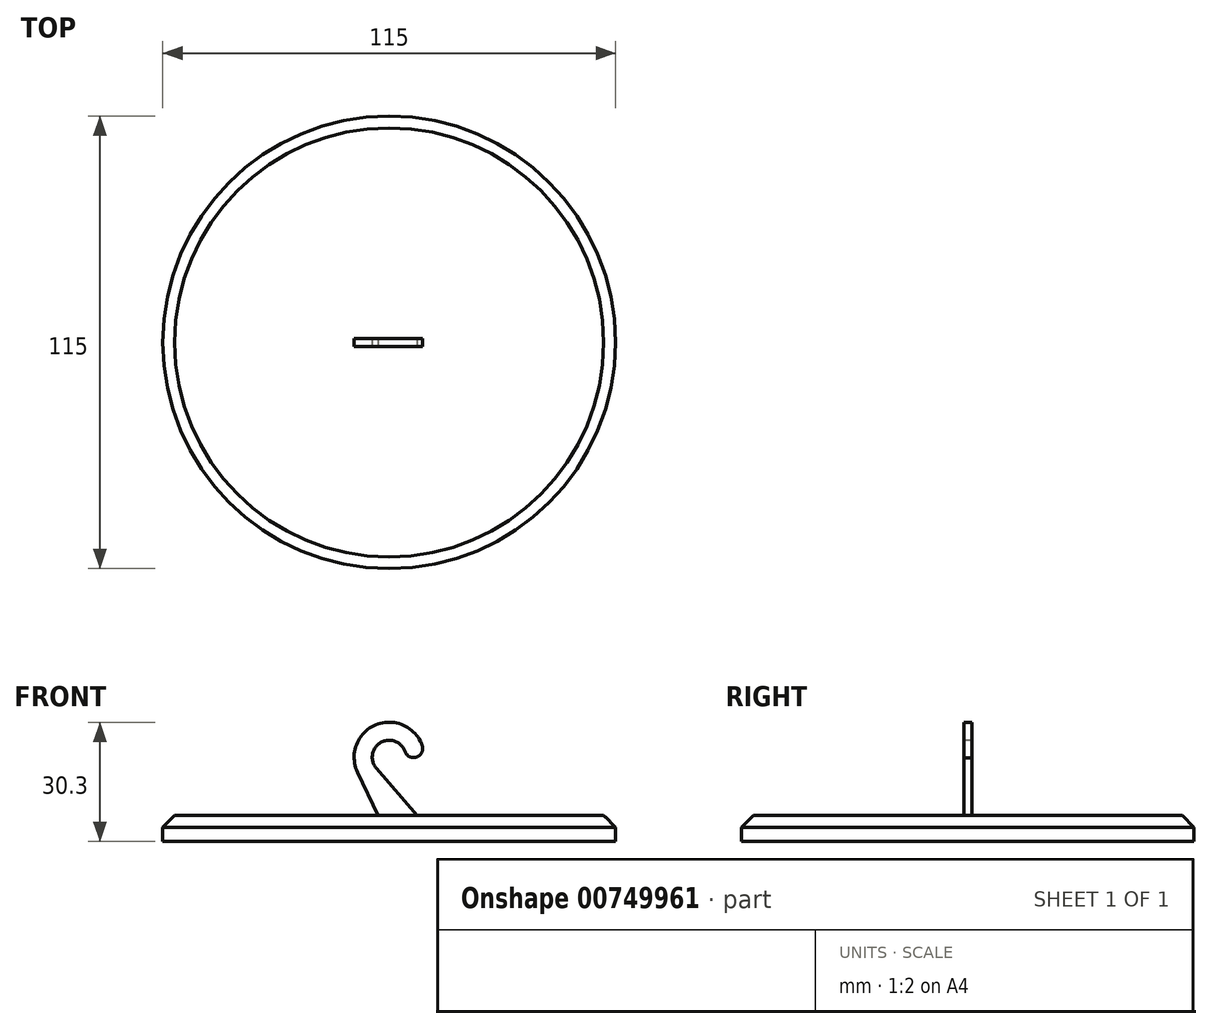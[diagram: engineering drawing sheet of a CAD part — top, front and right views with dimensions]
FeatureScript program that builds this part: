
annotation { "Feature Type Name" : "Feature", "Feature Type Description" : "" }
export const myFeature = defineFeature(function(context is Context, id is Id, definition is map)
    precondition{}
    {
        {
            var Q0;
            Q0=qCreatedBy(makeId("Top.planeOp"),FACE);
            var sketch = newSketch(context, id + "F0", { "sketchPlane" : qUnion([Q0])});
            skCircle(sketch, "E0", {"center": v(0, 0) * mm, "radius": 57.5 * mm});
            skSolve(sketch);
        }
        {
            var Q0;
            Q0=makeQuery(id+"F0.imprint","IMPRINT",FACE,{"disambiguationData":[TD([[makeQuery(id+"F0.imprint","IMPRINT",EDGE,{"derivedFrom":sQuery(id+"F0.wireOp",EDGE,"E0")}),1.0]])]});
            extrude(context, id + "F1", {"entities" : qUnion([Q0]), "depth" : 6.6 * mm, "offsetDistance" : 25 * mm});
        }
        {
            var Q0;
            Q0=makeQuery(id+"F1.opExtrude","CAP_EDGE",EDGE,{"disambiguationData":[OSD([sQuery(id+"F0.wireOp",EDGE,"E0")])],"isStart":false});
            chamfer(context, id + "F2", {"entities" : qUnion([Q0]), "width" : 3 * mm, "tangentPropagation" : true});
        }
        {
            var Q0;
            Q0=makeQuery(id+"F1.opExtrude","CAP_FACE",FACE,{"disambiguationData":[OSD([sQuery(id+"F0.wireOp",EDGE,"E0")])],"isStart":false});
            var sketch = newSketch(context, id + "F3", { "sketchPlane" : qUnion([Q0])});
            skLineSegment(sketch, "E1.bottom", {"start": v(-8.9, 1) * mm, "end": v(8.9, 1) * mm});
            skLineSegment(sketch, "E1.top", {"start": v(-8.9, -1) * mm, "end": v(8.9, -1) * mm});
            skLineSegment(sketch, "E1.left", {"start": v(-8.9, 1) * mm, "end": v(-8.9, -1) * mm});
            skLineSegment(sketch, "E1.right", {"start": v(8.9, 1) * mm, "end": v(8.9, -1) * mm});
            skLineSegment(sketch, "E2", {"start": v(0, 0) * mm, "end": v(0, 1) * mm, "construction": true});
            skLineSegment(sketch, "E3", {"start": v(0, 0) * mm, "end": v(-8.9, 0) * mm, "construction": true});
            skSolve(sketch);
        }
        {
            var Q0;
            Q0=makeQuery(id+"F3.imprint","IMPRINT",FACE,{"disambiguationData":[TD([[makeQuery(id+"F3.imprint","IMPRINT",EDGE,{"derivedFrom":sQuery(id+"F3.wireOp",EDGE,"E1.bottom")}),-1.0]])]});
            extrude(context, id + "F4", {"entities" : qUnion([Q0]), "operationType" : NewBodyOperationType.ADD, "depth" : 23.7 * mm, "offsetDistance" : 25 * mm});
        }
        {
            var Q0;
            Q0=makeQuery(id+"F4.opExtrude","SWEPT_FACE",FACE,{"disambiguationData":[OSD([sQuery(id+"F3.wireOp",EDGE,"E1.top")])]});
            var sketch = newSketch(context, id + "F5", { "sketchPlane" : qUnion([Q0])});
            skCircle(sketch, "E4", {"center": v(0, 21.4) * mm, "radius": 8.9 * mm});
            skCircle(sketch, "E5", {"center": v(0, 21.4) * mm, "radius": 4.3 * mm});
            skCircle(sketch, "E6", {"center": v(6.23, 23.59) * mm, "radius": 2.3 * mm});
            skLineSegment(sketch, "E7", {"start": v(-3.26, 18.6) * mm, "end": v(7.04, 6.6) * mm});
            skLineSegment(sketch, "E8", {"start": v(-8.03, 17.56) * mm, "end": v(-2.8, 6.6) * mm});
            skSolve(sketch);
        }
        {
            var Q0;
            {var subQ0=sQuery(id+"F5.wireOp",EDGE,"E7");var subQ3=sQuery(id+"F3.wireOp",EDGE,"E1.top");var subQ6=makeQuery(id+"F4.opExtrude","CAP_EDGE",EDGE,{"disambiguationData":[OSD([subQ3])],"isStart":true});var subQ8=makeQuery(id+"F5.imprint","INTERSECT",VERTEX,{"derivedFrom":[subQ6,subQ0]});Q0=makeQuery(id+"F5.imprint","IMPRINT",FACE,{"disambiguationData":[TD([[makeQuery(id+"F5.imprint","IMPRINT",EDGE,{"disambiguationData":[TD([[subQ8,1.0]])],"derivedFrom":subQ0}),1.0]])]});}
            var Q1;
            {var subQ3=sQuery(id+"F5.wireOp",EDGE,"E5");var subQ5=sQuery(id+"F5.wireOp",EDGE,"E7");var subQ6=makeQuery(id+"F5.imprint","INTERSECT",VERTEX,{"derivedFrom":[subQ3,subQ5]});Q1=makeQuery(id+"F5.imprint","IMPRINT",FACE,{"disambiguationData":[TD([[makeQuery(id+"F5.imprint","IMPRINT",EDGE,{"disambiguationData":[TD([[subQ6,-1.0]])],"derivedFrom":subQ3}),-1.0]])]});}
            var Q2;
            {var subQ0=sQuery(id+"F5.wireOp",EDGE,"E5");var subQ1=makeQuery(id+"F5.imprint","INTERSECT",VERTEX,{"derivedFrom":[subQ0,sQuery(id+"F5.wireOp",EDGE,"E7")]});Q2=makeQuery(id+"F5.imprint","IMPRINT",FACE,{"disambiguationData":[TD([[makeQuery(id+"F5.imprint","IMPRINT",EDGE,{"disambiguationData":[TD([[subQ1,1.0]])],"derivedFrom":subQ0}),1.0]])]});}
            var Q3;
            {var subQ0=sQuery(id+"F5.wireOp",EDGE,"E4");var subQ1=makeQuery(id+"F5.imprint","INTERSECT",VERTEX,{"derivedFrom":[subQ0,sQuery(id+"F5.wireOp",EDGE,"E6")]});Q3=makeQuery(id+"F5.imprint","IMPRINT",FACE,{"disambiguationData":[TD([[makeQuery(id+"F5.imprint","IMPRINT",EDGE,{"disambiguationData":[TD([[subQ1,-1.0]])],"derivedFrom":subQ0}),-1.0]])]});}
            var Q4;
            {var subQ0=sQuery(id+"F5.wireOp",EDGE,"E4");var subQ1=sQuery(id+"F3.wireOp",EDGE,"E1.top");var subQ2=makeQuery(id+"F4.opExtrude","CAP_EDGE",EDGE,{"disambiguationData":[OSD([subQ1])],"isStart":false});var subQ3=makeQuery(id+"F5.imprint","INTERSECT",VERTEX,{"derivedFrom":[subQ2,subQ0]});Q4=makeQuery(id+"F5.imprint","IMPRINT",FACE,{"disambiguationData":[TD([[makeQuery(id+"F5.imprint","IMPRINT",EDGE,{"disambiguationData":[TD([[subQ3,-1.0]])],"derivedFrom":subQ0}),-1.0]])]});}
            var Q5;
            {var subQ0=sQuery(id+"F5.wireOp",EDGE,"E8");Q5=makeQuery(id+"F5.imprint","IMPRINT",FACE,{"disambiguationData":[TD([[makeQuery(id+"F5.imprint","IMPRINT",EDGE,{"derivedFrom":subQ0}),-1.0]])]});}
            extrude(context, id + "F6", {"entities" : qUnion([Q0, Q1, Q2, Q3, Q4, Q5]), "operationType" : NewBodyOperationType.REMOVE, "endBound" : BoundingType.UP_TO_NEXT, "oppositeDirection" : true, "depth" : 25 * mm, "offsetDistance" : 25 * mm});
        }
    });
